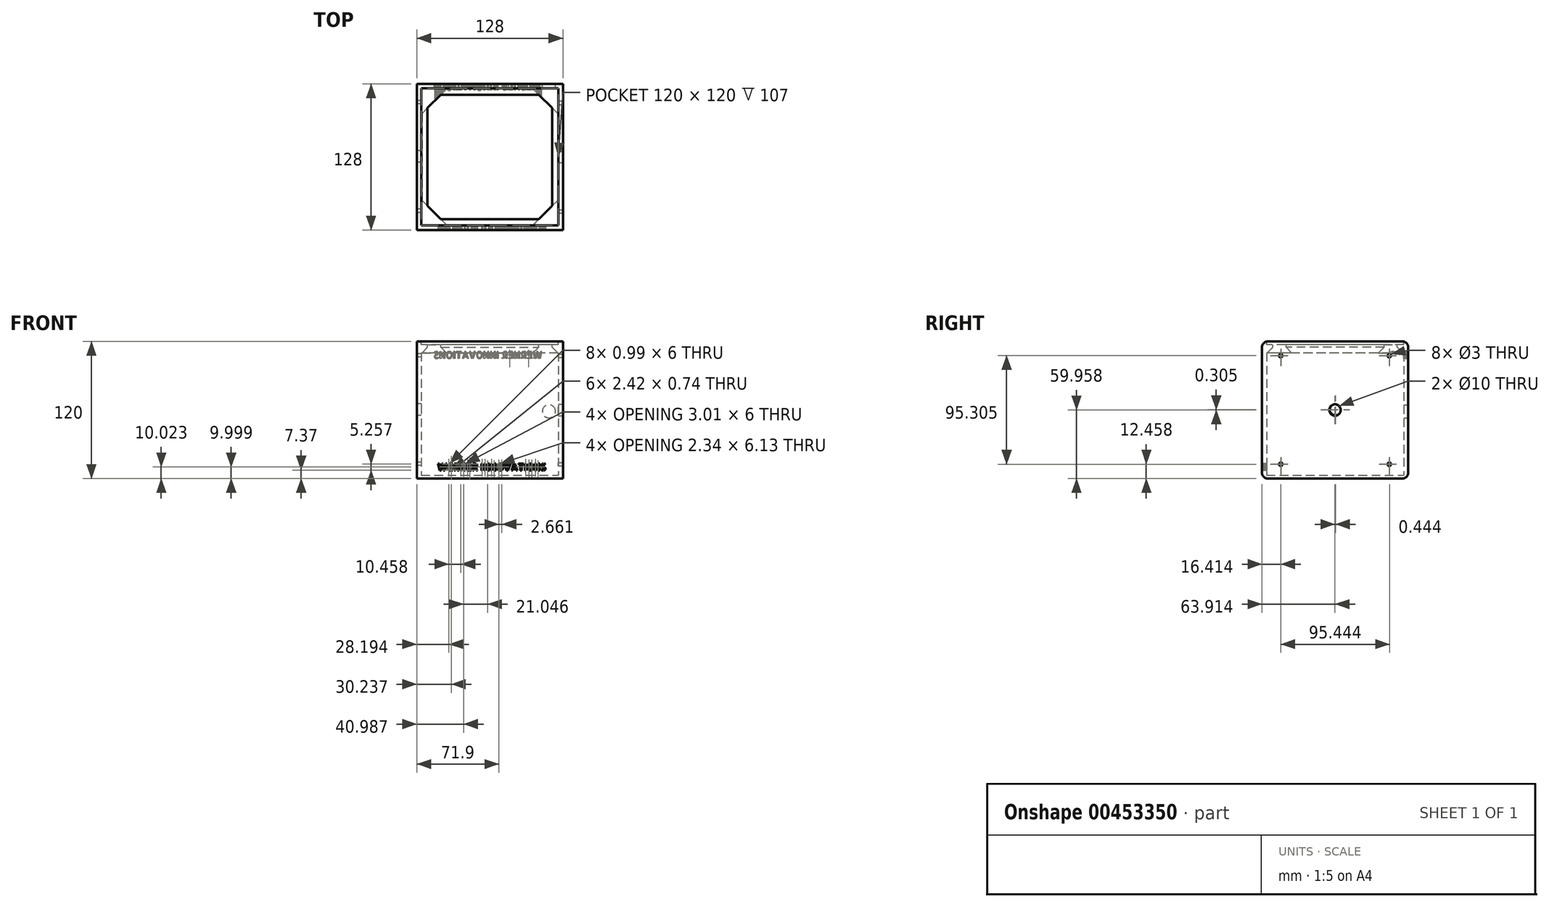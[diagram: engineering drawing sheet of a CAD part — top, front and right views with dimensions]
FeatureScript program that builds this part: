
annotation { "Feature Type Name" : "Feature", "Feature Type Description" : "" }
export const myFeature = defineFeature(function(context is Context, id is Id, definition is map)
    precondition{}
    {
        {
            var Q0;
            Q0=qCreatedBy(makeId("Top.planeOp"),FACE);
            var sketch = newSketch(context, id + "F0", { "sketchPlane" : qUnion([Q0])});
            skLineSegment(sketch, "E0.bottom", {"start": v(60, 60) * mm, "end": v(-60, 60) * mm});
            skLineSegment(sketch, "E0.top", {"start": v(60, -60) * mm, "end": v(-60, -60) * mm});
            skLineSegment(sketch, "E0.left", {"start": v(60, 60) * mm, "end": v(60, -60) * mm});
            skLineSegment(sketch, "E0.right", {"start": v(-60, 60) * mm, "end": v(-60, -60) * mm});
            skPoint(sketch, "E0.middle", {"position": v(0, 0) * mm});
            skLineSegment(sketch, "E1.0", {"start": v(64, 64) * mm, "end": v(-64, 64) * mm});
            skLineSegment(sketch, "E1.1", {"start": v(64, 64) * mm, "end": v(64, -64) * mm});
            skLineSegment(sketch, "E1.2", {"start": v(64, -64) * mm, "end": v(-64, -64) * mm});
            skLineSegment(sketch, "E1.3", {"start": v(-64, 64) * mm, "end": v(-64, -64) * mm});
            skSolve(sketch);
        }
        {
            var Q0;
            Q0=makeQuery(id+"F0.imprint","IMPRINT",FACE,{"disambiguationData":[TD([[makeQuery(id+"F0.imprint","IMPRINT",EDGE,{"derivedFrom":sQuery(id+"F0.wireOp",EDGE,"E0.bottom")}),1.0]])]});
            var Q1;
            Q1=makeQuery(id+"F0.imprint","IMPRINT",FACE,{"disambiguationData":[TD([[makeQuery(id+"F0.imprint","IMPRINT",EDGE,{"derivedFrom":sQuery(id+"F0.wireOp",EDGE,"E0.bottom")}),-1.0]])]});
            extrude(context, id + "F1", {"entities" : qUnion([Q0, Q1]), "depth" : 3 * mm});
        }
        {
            var Q0;
            Q0 = qSketchRegion(id + "F0", true);
            extrude(context, id + "F2", {"entities" : qUnion([Q0]), "operationType" : NewBodyOperationType.ADD, "depth" : 120 * mm});
        }
        {
            var Q0;
            Q0=makeQuery(id+"F2.opExtrude","CAP_FACE",FACE,{"disambiguationData":[OSD([sQuery(id+"F0.wireOp",EDGE,"E0.bottom"),sQuery(id+"F0.wireOp",EDGE,"E0.top"),sQuery(id+"F0.wireOp",EDGE,"E0.left"),sQuery(id+"F0.wireOp",EDGE,"E0.right"),sQuery(id+"F0.wireOp",EDGE,"E1.0"),sQuery(id+"F0.wireOp",EDGE,"E1.1"),sQuery(id+"F0.wireOp",EDGE,"E1.2"),sQuery(id+"F0.wireOp",EDGE,"E1.3")])],"isStart":false});
            var sketch = newSketch(context, id + "F3", { "sketchPlane" : qUnion([Q0])});
            skLineSegment(sketch, "E2.0", {"start": v(42.87, 54.5) * mm, "end": v(-42.87, 54.5) * mm});
            skLineSegment(sketch, "E2.1", {"start": v(54.5, 42.87) * mm, "end": v(54.5, -42.87) * mm});
            skLineSegment(sketch, "E2.2", {"start": v(42.87, -54.5) * mm, "end": v(-42.87, -54.5) * mm});
            skLineSegment(sketch, "E2.3", {"start": v(-54.5, 42.87) * mm, "end": v(-54.5, -42.87) * mm});
            skLineSegment(sketch, "E3.0", {"start": v(-65, -65) * mm, "end": v(65, -65) * mm});
            skLineSegment(sketch, "E3.1", {"start": v(-65, 65) * mm, "end": v(-65, -65) * mm});
            skLineSegment(sketch, "E3.2", {"start": v(65, 65) * mm, "end": v(-65, 65) * mm});
            skLineSegment(sketch, "E3.3", {"start": v(65, -65) * mm, "end": v(65, 65) * mm});
            skLineSegment(sketch, "E4", {"start": v(-54.5, 42.87) * mm, "end": v(-42.87, 54.5) * mm});
            skLineSegment(sketch, "E5", {"start": v(0, 69.57) * mm, "end": v(0, -76.5) * mm, "construction": true});
            skLineSegment(sketch, "E6", {"start": v(-74.42, 0) * mm, "end": v(73.6, 0) * mm, "construction": true});
            skPoint(sketch, "E6.endSnap0", {"position": v(60, 0) * mm});
            skLineSegment(sketch, "E7.MirrorCS", {"start": v(54.5, 42.87) * mm, "end": v(42.87, 54.5) * mm});
            skLineSegment(sketch, "E8.MirrorCS", {"start": v(54.5, -42.87) * mm, "end": v(42.87, -54.5) * mm});
            skLineSegment(sketch, "E9.MirrorCS", {"start": v(-54.5, -42.87) * mm, "end": v(-42.87, -54.5) * mm});
            skSolve(sketch);
        }
        {
            var Q0;
            Q0=makeQuery(id+"F3.imprint","IMPRINT",FACE,{"disambiguationData":[TD([[makeQuery(id+"F3.imprint","IMPRINT",EDGE,{"derivedFrom":sQuery(id+"F3.wireOp",EDGE,"E2.0")}),-1.0]])]});
            extrude(context, id + "F4", {"entities" : qUnion([Q0]), "operationType" : NewBodyOperationType.ADD, "depth" : -10 * mm});
        }
        {
            var Q0;
            Q0=makeQuery(id+"F3.imprint","IMPRINT",FACE,{"disambiguationData":[TD([[makeQuery(id+"F3.imprint","IMPRINT",EDGE,{"derivedFrom":sQuery(id+"F3.wireOp",EDGE,"E2.0")}),-1.0]])]});
            extrude(context, id + "F5", {"entities" : qUnion([Q0]), "operationType" : NewBodyOperationType.REMOVE, "oppositeDirection" : true, "depth" : 3 * mm});
        }
        {
            var Q0;
            Q0=makeQuery(id+"F4.opExtrude","CAP_EDGE",EDGE,{"disambiguationData":[OSD([sQuery(id+"F3.wireOp",EDGE,"E2.0")])],"isStart":false});
            var Q1;
            Q1=makeQuery(id+"F4.opExtrude","CAP_EDGE",EDGE,{"disambiguationData":[OSD([sQuery(id+"F3.wireOp",EDGE,"E2.3")])],"isStart":false});
            var Q2;
            Q2=makeQuery(id+"F4.opExtrude","CAP_EDGE",EDGE,{"disambiguationData":[OSD([sQuery(id+"F3.wireOp",EDGE,"E2.1")])],"isStart":false});
            var Q3;
            Q3=makeQuery(id+"F4.opExtrude","CAP_EDGE",EDGE,{"disambiguationData":[OSD([sQuery(id+"F3.wireOp",EDGE,"E2.2")])],"isStart":false});
            chamfer(context, id + "F6", {"entities" : qUnion([Q0, Q1, Q2, Q3]), "width" : 5 * mm, "tangentPropagation" : true});
        }
        {
            var Q0;
            {var subQ0=sQuery(id+"F0.wireOp",EDGE,"E1.1");Q0=makeQuery(id+"F2.boolean.opBoolean","MERGE",FACE,{"derivedFrom":[makeQuery(id+"F1.opExtrude","SWEPT_FACE",FACE,{"disambiguationData":[OSD([subQ0])]}),makeQuery(id+"F2.opExtrude","SWEPT_FACE",FACE,{"disambiguationData":[OSD([subQ0])]})]});}
            var sketch = newSketch(context, id + "F7", { "sketchPlane" : qUnion([Q0])});
            skLineSegment(sketch, "E10", {"start": v(0, 0) * mm, "end": v(0, 131.57) * mm, "construction": true});
            skLineSegment(sketch, "E11", {"start": v(-64, 60) * mm, "end": v(64, 60) * mm, "construction": true});
            skLineSegment(sketch, "E12", {"start": v(-0.09, -0.04) * mm, "end": v(-0.09, 119.96) * mm, "construction": true});
            skCircle(sketch, "E13", {"center": v(-0.09, 59.96) * mm, "radius": 5 * mm});
            skLineSegment(sketch, "E14.bottom", {"start": v(47.41, 107.46) * mm, "end": v(-47.59, 107.46) * mm, "construction": true});
            skLineSegment(sketch, "E14.top", {"start": v(47.41, 12.46) * mm, "end": v(-47.59, 12.46) * mm, "construction": true});
            skLineSegment(sketch, "E14.left", {"start": v(47.41, 107.46) * mm, "end": v(47.41, 12.46) * mm, "construction": true});
            skLineSegment(sketch, "E14.right", {"start": v(-47.59, 107.46) * mm, "end": v(-47.59, 12.46) * mm, "construction": true});
            skCircle(sketch, "E15", {"center": v(-47.59, 107.46) * mm, "radius": 1.5 * mm});
            skCircle(sketch, "E16", {"center": v(47.41, 107.46) * mm, "radius": 1.5 * mm});
            skCircle(sketch, "E17", {"center": v(47.41, 12.46) * mm, "radius": 1.5 * mm});
            skCircle(sketch, "E18", {"center": v(-47.59, 12.46) * mm, "radius": 1.5 * mm});
            skSolve(sketch);
        }
        {
            var Q0;
            Q0 = qSketchRegion(id + "F7", true);
            extrude(context, id + "F8", {"entities" : qUnion([Q0]), "operationType" : NewBodyOperationType.REMOVE, "oppositeDirection" : true, "depth" : 4 * mm});
        }
        {
            var Q0;
            {var subQ0=sQuery(id+"F0.wireOp",EDGE,"E1.3");Q0=makeQuery(id+"F2.boolean.opBoolean","MERGE",FACE,{"derivedFrom":[makeQuery(id+"F1.opExtrude","SWEPT_FACE",FACE,{"disambiguationData":[OSD([subQ0])]}),makeQuery(id+"F2.opExtrude","SWEPT_FACE",FACE,{"disambiguationData":[OSD([subQ0])]})]});}
            var sketch = newSketch(context, id + "F9", { "sketchPlane" : qUnion([Q0])});
            skLineSegment(sketch, "E19", {"start": v(0, 0) * mm, "end": v(0, 120) * mm, "construction": true});
            skLineSegment(sketch, "E20", {"start": v(-64, 60) * mm, "end": v(64, 60) * mm, "construction": true});
            skLineSegment(sketch, "E21", {"start": v(-0.36, 0.26) * mm, "end": v(-0.36, 120.26) * mm, "construction": true});
            skCircle(sketch, "E22", {"center": v(-0.36, 60.26) * mm, "radius": 5 * mm});
            skLineSegment(sketch, "E23.bottom", {"start": v(47.14, 107.76) * mm, "end": v(-47.86, 107.76) * mm, "construction": true});
            skLineSegment(sketch, "E23.top", {"start": v(47.14, 12.76) * mm, "end": v(-47.86, 12.76) * mm, "construction": true});
            skLineSegment(sketch, "E23.left", {"start": v(47.14, 107.76) * mm, "end": v(47.14, 12.76) * mm, "construction": true});
            skLineSegment(sketch, "E23.right", {"start": v(-47.86, 107.76) * mm, "end": v(-47.86, 12.76) * mm, "construction": true});
            skCircle(sketch, "E24", {"center": v(-47.86, 107.76) * mm, "radius": 1.5 * mm});
            skCircle(sketch, "E25", {"center": v(47.14, 107.76) * mm, "radius": 1.5 * mm});
            skCircle(sketch, "E26", {"center": v(47.14, 12.76) * mm, "radius": 1.5 * mm});
            skCircle(sketch, "E27", {"center": v(-47.86, 12.76) * mm, "radius": 1.5 * mm});
            skSolve(sketch);
        }
        {
            var Q0;
            Q0=makeQuery(id+"F9.imprint","IMPRINT",FACE,{"disambiguationData":[TD([[makeQuery(id+"F9.imprint","IMPRINT",EDGE,{"derivedFrom":sQuery(id+"F9.wireOp",EDGE,"E22")}),1.0]])]});
            var Q1;
            Q1=makeQuery(id+"F9.imprint","IMPRINT",FACE,{"disambiguationData":[TD([[makeQuery(id+"F9.imprint","IMPRINT",EDGE,{"derivedFrom":sQuery(id+"F9.wireOp",EDGE,"E27")}),1.0]])]});
            var Q2;
            Q2=makeQuery(id+"F9.imprint","IMPRINT",FACE,{"disambiguationData":[TD([[makeQuery(id+"F9.imprint","IMPRINT",EDGE,{"derivedFrom":sQuery(id+"F9.wireOp",EDGE,"E26")}),1.0]])]});
            var Q3;
            Q3=makeQuery(id+"F9.imprint","IMPRINT",FACE,{"disambiguationData":[TD([[makeQuery(id+"F9.imprint","IMPRINT",EDGE,{"derivedFrom":sQuery(id+"F9.wireOp",EDGE,"E25")}),1.0]])]});
            var Q4;
            Q4=makeQuery(id+"F9.imprint","IMPRINT",FACE,{"disambiguationData":[TD([[makeQuery(id+"F9.imprint","IMPRINT",EDGE,{"derivedFrom":sQuery(id+"F9.wireOp",EDGE,"E24")}),1.0]])]});
            extrude(context, id + "F10", {"entities" : qUnion([Q0, Q1, Q2, Q3, Q4]), "operationType" : NewBodyOperationType.REMOVE, "oppositeDirection" : true, "depth" : 4 * mm});
        }
        {
            var Q0;
            Q0=makeQuery(id+"F2.opExtrude","CAP_EDGE",EDGE,{"disambiguationData":[OSD([sQuery(id+"F0.wireOp",EDGE,"E1.0")])],"isStart":false});
            var Q1;
            Q1=makeQuery(id+"F2.opExtrude","CAP_EDGE",EDGE,{"disambiguationData":[OSD([sQuery(id+"F0.wireOp",EDGE,"E1.2")])],"isStart":false});
            var Q2;
            Q2=makeQuery(id+"F1.opExtrude","CAP_EDGE",EDGE,{"disambiguationData":[OSD([sQuery(id+"F0.wireOp",EDGE,"E1.0")])],"isStart":true});
            var Q3;
            Q3=makeQuery(id+"F1.opExtrude","CAP_EDGE",EDGE,{"disambiguationData":[OSD([sQuery(id+"F0.wireOp",EDGE,"E1.2")])],"isStart":true});
            fillet(context, id + "F11", {"entities" : qUnion([Q0, Q1, Q2, Q3]), "radius" : 5 * mm, "tangentPropagation" : true, "allowEdgeOverflow" : false});
        }
        {
            var Q0;
            {var subQ0=sQuery(id+"F0.wireOp",EDGE,"E1.2");Q0=makeQuery(id+"F2.boolean.opBoolean","MERGE",FACE,{"derivedFrom":[makeQuery(id+"F1.opExtrude","SWEPT_FACE",FACE,{"disambiguationData":[OSD([subQ0])]}),makeQuery(id+"F2.opExtrude","SWEPT_FACE",FACE,{"disambiguationData":[OSD([subQ0])]})]});}
            var sketch = newSketch(context, id + "F12", { "sketchPlane" : qUnion([Q0])});
            skText(sketch, "E28", { "text": "WERNER INNOVATIONS", "fontName": "AllertaStencil-Regular.ttf"});
            const initialGuessF12  = {"E28": [-0.04597, 0.007, 1, 0, 0.006]};
            skSetInitialGuess(sketch, initialGuessF12);
            skSolve(sketch);
        }
        {
            var Q0;
            Q0 = qSketchRegion(id + "F12", true);
            extrude(context, id + "F13", {"entities" : qUnion([Q0]), "operationType" : NewBodyOperationType.REMOVE, "oppositeDirection" : true, "depth" : 5 * mm});
        }
        {
            var Q0;
            {var subQ0=sQuery(id+"F0.wireOp",EDGE,"E1.0");Q0=makeQuery(id+"F2.boolean.opBoolean","MERGE",FACE,{"derivedFrom":[makeQuery(id+"F1.opExtrude","SWEPT_FACE",FACE,{"disambiguationData":[OSD([subQ0])]}),makeQuery(id+"F2.opExtrude","SWEPT_FACE",FACE,{"disambiguationData":[OSD([subQ0])]})]});}
            var sketch = newSketch(context, id + "F14", { "sketchPlane" : qUnion([Q0])});
            skText(sketch, "E29", { "text": "WERNER INNOVATIONS", "fontName": "AllertaStencil-Regular.ttf"});
            const initialGuessF14  = {"E29": [-0.04607, 0.1051, 1, 0, 0.006]};
            skSetInitialGuess(sketch, initialGuessF14);
            skSolve(sketch);
        }
        {
            var Q0;
            Q0 = qSketchRegion(id + "F14", true);
            var Q1;
            Q1=makeQuery(id+"F3nrf4awNcNfk3M_1.opChamfer","BLEND_FACE",FACE,{"disambiguationData":[OSD([sQuery(id+"F3.wireOp",EDGE,"E7.MirrorCS")])]});
            extrude(context, id + "F15", {"entities" : qUnion([Q0, Q1]), "operationType" : NewBodyOperationType.REMOVE, "oppositeDirection" : true, "depth" : 15 * mm});
        }
        {
            var Q0;
            {var subQ0=sQuery(id+"F0.wireOp",EDGE,"E1.0");Q0=makeQuery(id+"F2.boolean.opBoolean","MERGE",FACE,{"derivedFrom":[makeQuery(id+"F1.opExtrude","SWEPT_FACE",FACE,{"disambiguationData":[OSD([subQ0])]}),makeQuery(id+"F2.opExtrude","SWEPT_FACE",FACE,{"disambiguationData":[OSD([subQ0])]})]});}
            var sketch = newSketch(context, id + "F16", { "sketchPlane" : qUnion([Q0])});
            skCircle(sketch, "E30", {"center": v(-51.7, 58.81) * mm, "radius": 5.75 * mm});
            skSolve(sketch);
        }
        {
            var Q0;
            Q0 = qSketchRegion(id + "F16", true);
            extrude(context, id + "F17", {"entities" : qUnion([Q0]), "operationType" : NewBodyOperationType.REMOVE, "oppositeDirection" : true, "depth" : 4 * mm});
        }
    });
